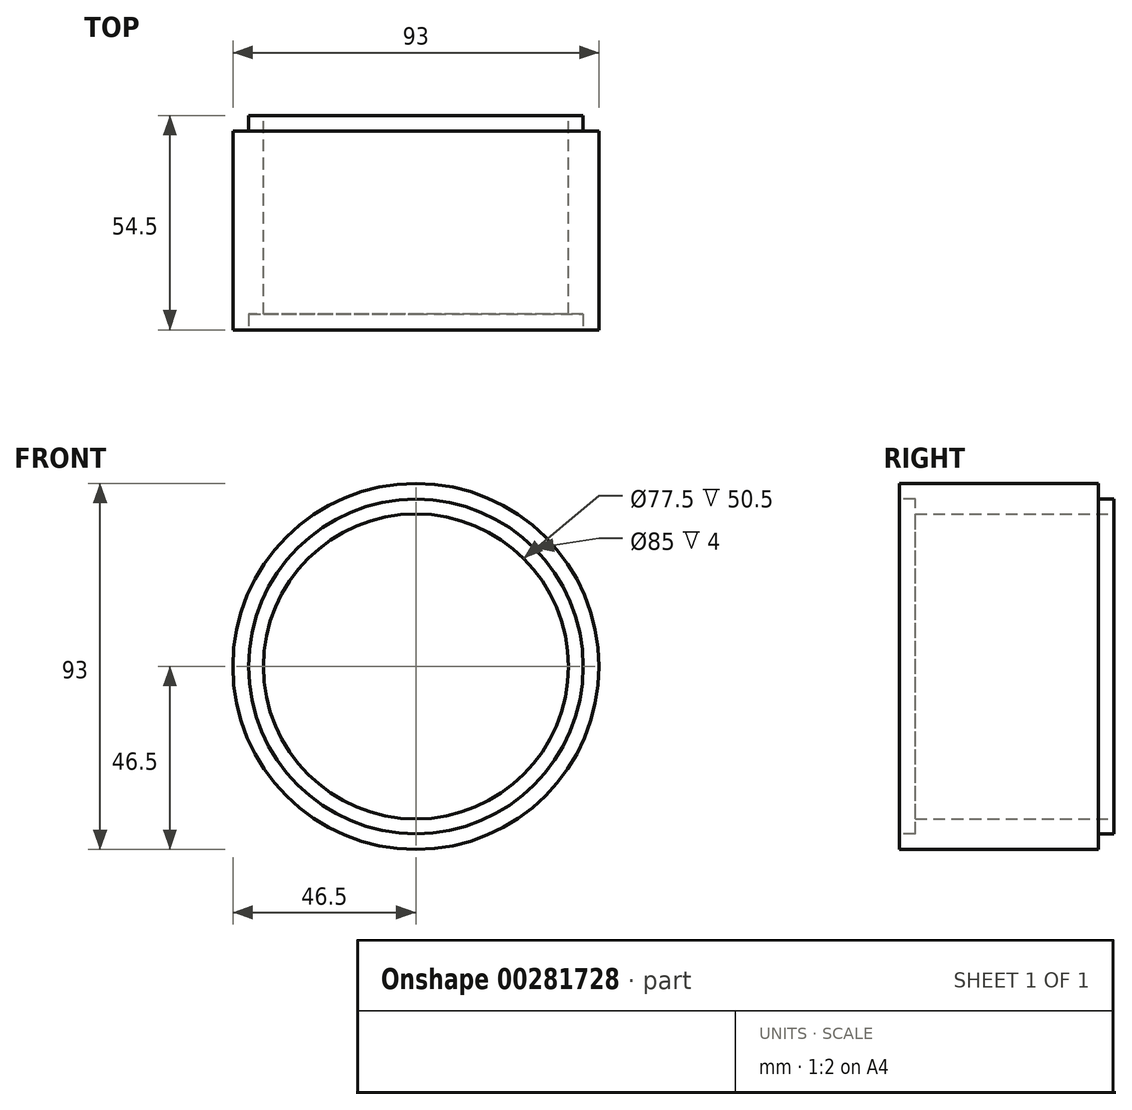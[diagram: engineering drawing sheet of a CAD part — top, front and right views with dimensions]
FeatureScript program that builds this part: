
annotation { "Feature Type Name" : "Feature", "Feature Type Description" : "" }
export const myFeature = defineFeature(function(context is Context, id is Id, definition is map)
    precondition{}
    {
        {
            assignVariable(context, id + "F0", {"name" : "SR_Length", "anyValue" : 50.5});
        }
        {
            assignVariable(context, id + "F1", {"name" : "SR_ThreadLength", "anyValue" : 4});
        }
        {
            var Q0;
            Q0=qCreatedBy(makeId("Front.planeOp"),FACE);
            var sketch = newSketch(context, id + "F2", { "sketchPlane" : qUnion([Q0])});
            skCircle(sketch, "E0", {"center": v(0, 0) * mm, "radius": 46.5 * mm});
            skCircle(sketch, "E1", {"center": v(0, 0) * mm, "radius": 38.75 * mm});
            skCircle(sketch, "E2", {"center": v(0, 0) * mm, "radius": 42.5 * mm});
            skSolve(sketch);
        }
        {
            var Q0;
            Q0=makeQuery(id+"F2.imprint","IMPRINT",FACE,{"disambiguationData":[TD([[makeQuery(id+"F2.imprint","IMPRINT",EDGE,{"derivedFrom":sQuery(id+"F2.wireOp",EDGE,"E1")}),-1.0]])]});
            var Q1;
            Q1=makeQuery(id+"F2.imprint","IMPRINT",FACE,{"disambiguationData":[TD([[makeQuery(id+"F2.imprint","IMPRINT",EDGE,{"derivedFrom":sQuery(id+"F2.wireOp",EDGE,"E0")}),1.0]])]});
            extrude(context, id + "F3", {"entities" : qUnion([Q0, Q1]), "depth" : (getVariable(context, 'SR_Length') + getVariable(context, 'SR_ThreadLength')) * mm, "offsetDistance" : 25 * mm});
        }
        {
            var Q0;
            Q0=makeQuery(id+"F2.imprint","IMPRINT",FACE,{"disambiguationData":[TD([[makeQuery(id+"F2.imprint","IMPRINT",EDGE,{"derivedFrom":sQuery(id+"F2.wireOp",EDGE,"E0")}),1.0]])]});
            extrude(context, id + "F4", {"entities" : qUnion([Q0]), "operationType" : NewBodyOperationType.REMOVE, "depth" : (getVariable(context, 'SR_ThreadLength')) * mm, "offsetDistance" : 25 * mm});
        }
        {
            var Q0;
            Q0=makeQuery(id+"F3.opExtrude","CAP_FACE",FACE,{"disambiguationData":[OSD([sQuery(id+"F2.wireOp",EDGE,"E0"),sQuery(id+"F2.wireOp",EDGE,"E1")])],"isStart":false});
            var sketch = newSketch(context, id + "F5", { "sketchPlane" : qUnion([Q0])});
            skCircle(sketch, "E3", {"center": v(0, 0) * mm, "radius": 42.5 * mm});
            skSolve(sketch);
        }
        {
            var Q0;
            Q0=makeQuery(id+"F5.imprint","IMPRINT",FACE,{"disambiguationData":[TD([[makeQuery(id+"F5.imprint","IMPRINT",EDGE,{"derivedFrom":sQuery(id+"F5.wireOp",EDGE,"E3")}),1.0]])]});
            extrude(context, id + "F6", {"entities" : qUnion([Q0]), "operationType" : NewBodyOperationType.REMOVE, "oppositeDirection" : true, "depth" : (getVariable(context, 'SR_ThreadLength')) * mm, "offsetDistance" : 25 * mm});
        }
    });
